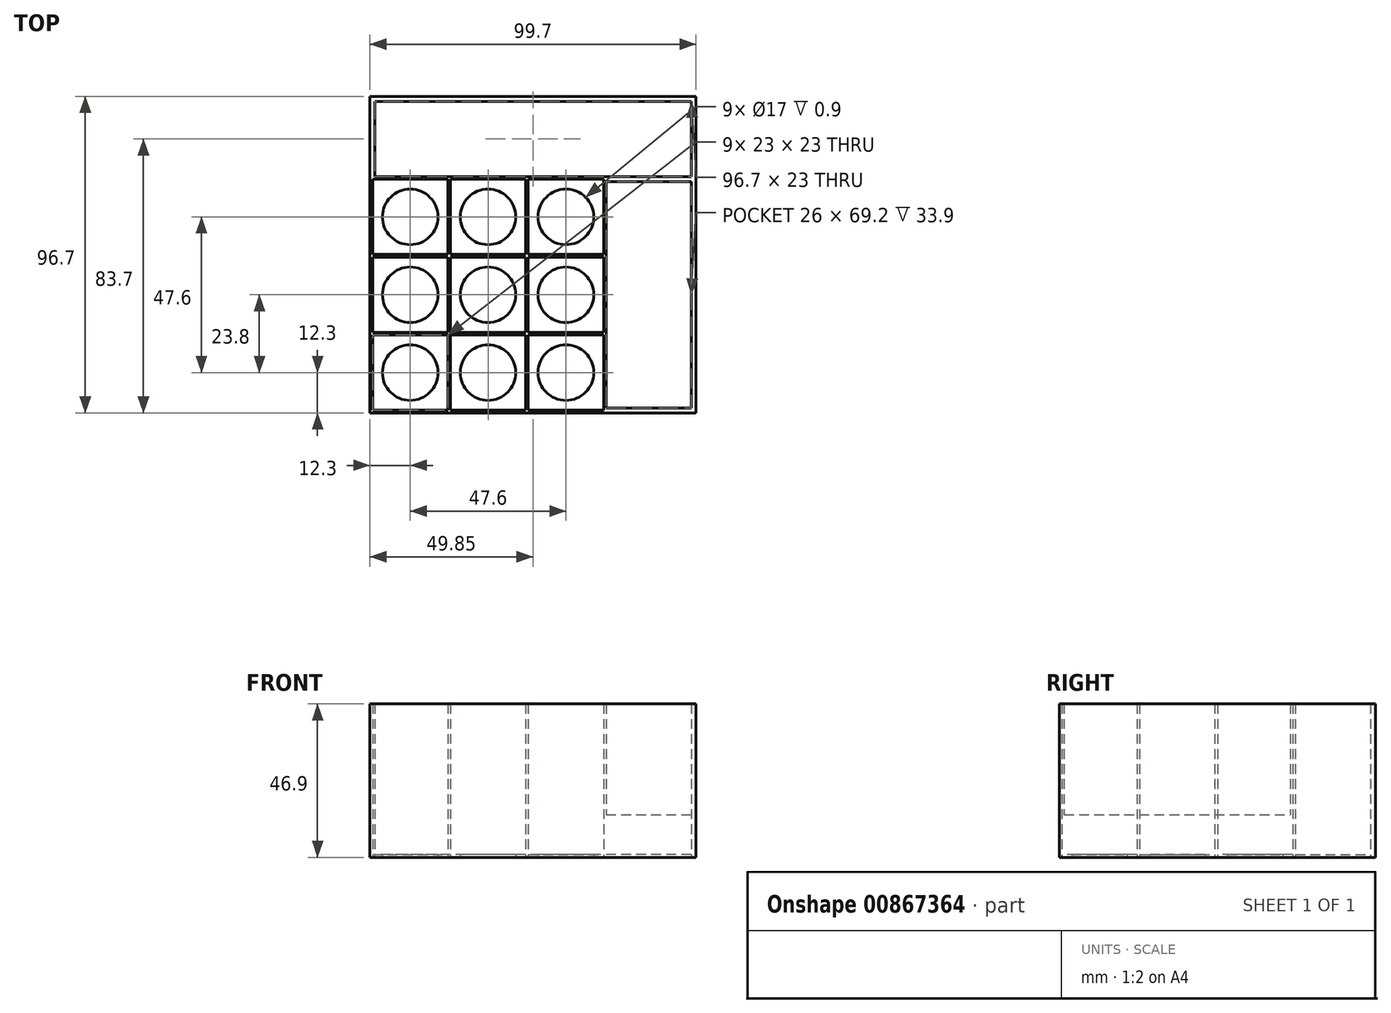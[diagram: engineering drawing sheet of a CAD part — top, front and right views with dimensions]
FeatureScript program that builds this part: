
annotation { "Feature Type Name" : "Feature", "Feature Type Description" : "" }
export const myFeature = defineFeature(function(context is Context, id is Id, definition is map)
    precondition{}
    {
        {
            var Q0;
            Q0=qCreatedBy(makeId("Top.planeOp"),FACE);
            var sketch = newSketch(context, id + "F0", { "sketchPlane" : qUnion([Q0])});
            skLineSegment(sketch, "E0", {"start": v(-36.1, 36.1) * mm, "end": v(-36.1, -36.1) * mm});
            skLineSegment(sketch, "E1", {"start": v(-36.1, -36.1) * mm, "end": v(36.1, -36.1) * mm});
            skLineSegment(sketch, "E2", {"start": v(36.1, -36.1) * mm, "end": v(36.1, 36.1) * mm});
            skLineSegment(sketch, "E3", {"start": v(36.1, 36.1) * mm, "end": v(-36.1, 36.1) * mm});
            skLineSegment(sketch, "E4.bottom", {"start": v(-35.3, 35.3) * mm, "end": v(-12.3, 35.3) * mm});
            skLineSegment(sketch, "E4.top", {"start": v(-35.3, 12.3) * mm, "end": v(-12.3, 12.3) * mm});
            skLineSegment(sketch, "E4.left", {"start": v(-35.3, 35.3) * mm, "end": v(-35.3, 12.3) * mm});
            skLineSegment(sketch, "E4.right", {"start": v(-12.3, 35.3) * mm, "end": v(-12.3, 12.3) * mm});
            skLineSegment(sketch, "E5", {"start": v(0, 86.02) * mm, "end": v(0, -32.75) * mm, "construction": true});
            skPoint(sketch, "E5.startSnap0", {"position": v(0, 36.1) * mm});
            skLineSegment(sketch, "E6", {"start": v(50.67, 0) * mm, "end": v(-45.02, 0) * mm, "construction": true});
            skPoint(sketch, "E6.startSnap0", {"position": v(36.1, 0) * mm});
            skPoint(sketch, "E7", {"position": v(0, 0) * mm});
            skLineSegment(sketch, "E8", {"start": v(-11.9, 47.3) * mm, "end": v(-11.9, -75.9) * mm, "construction": true});
            skLineSegment(sketch, "E9", {"start": v(-48.72, 11.9) * mm, "end": v(36.2, 11.9) * mm, "construction": true});
            skLineSegment(sketch, "E10.MirrorCS", {"start": v(-11.5, 35.3) * mm, "end": v(-11.5, 12.3) * mm});
            skLineSegment(sketch, "E11.MirrorCS", {"start": v(11.5, 35.3) * mm, "end": v(-11.5, 35.3) * mm});
            skLineSegment(sketch, "E12.MirrorCS", {"start": v(11.5, 35.3) * mm, "end": v(11.5, 12.3) * mm});
            skLineSegment(sketch, "E13.MirrorCS", {"start": v(11.5, 12.3) * mm, "end": v(-11.5, 12.3) * mm});
            skLineSegment(sketch, "E14", {"start": v(11.9, 49.65) * mm, "end": v(11.9, -75.25) * mm, "construction": true});
            skLineSegment(sketch, "E15.MirrorCS", {"start": v(12.3, 35.3) * mm, "end": v(12.3, 12.3) * mm});
            skLineSegment(sketch, "E16.MirrorCS", {"start": v(12.3, 35.3) * mm, "end": v(35.3, 35.3) * mm});
            skLineSegment(sketch, "E17.MirrorCS", {"start": v(35.3, 35.3) * mm, "end": v(35.3, 12.3) * mm});
            skLineSegment(sketch, "E18.MirrorCS", {"start": v(12.3, 12.3) * mm, "end": v(35.3, 12.3) * mm});
            skLineSegment(sketch, "E19.MirrorCS", {"start": v(-35.3, 11.5) * mm, "end": v(-12.3, 11.5) * mm});
            skLineSegment(sketch, "E20.MirrorCS", {"start": v(-12.3, -11.5) * mm, "end": v(-12.3, 11.5) * mm});
            skLineSegment(sketch, "E21.MirrorCS", {"start": v(-35.3, -11.5) * mm, "end": v(-12.3, -11.5) * mm});
            skLineSegment(sketch, "E22.MirrorCS", {"start": v(-35.3, -11.5) * mm, "end": v(-35.3, 11.5) * mm});
            skLineSegment(sketch, "E23.MirrorCS", {"start": v(-11.5, -11.5) * mm, "end": v(-11.5, 11.5) * mm});
            skLineSegment(sketch, "E24.MirrorCS", {"start": v(11.5, 11.5) * mm, "end": v(-11.5, 11.5) * mm});
            skLineSegment(sketch, "E25.MirrorCS", {"start": v(11.5, -11.5) * mm, "end": v(11.5, 11.5) * mm});
            skLineSegment(sketch, "E26.MirrorCS", {"start": v(11.5, -11.5) * mm, "end": v(-11.5, -11.5) * mm});
            skLineSegment(sketch, "E27.MirrorCS", {"start": v(12.3, -11.5) * mm, "end": v(35.3, -11.5) * mm});
            skLineSegment(sketch, "E28.MirrorCS", {"start": v(12.3, -11.5) * mm, "end": v(12.3, 11.5) * mm});
            skLineSegment(sketch, "E29.MirrorCS", {"start": v(12.3, 11.5) * mm, "end": v(35.3, 11.5) * mm});
            skLineSegment(sketch, "E30.MirrorCS", {"start": v(35.3, -11.5) * mm, "end": v(35.3, 11.5) * mm});
            skLineSegment(sketch, "E31", {"start": v(-45.02, -11.9) * mm, "end": v(46.48, -11.9) * mm, "construction": true});
            skLineSegment(sketch, "E32.MirrorCS", {"start": v(-35.3, -12.3) * mm, "end": v(-12.3, -12.3) * mm});
            skLineSegment(sketch, "E33.MirrorCS", {"start": v(-35.3, -12.3) * mm, "end": v(-35.3, -35.3) * mm});
            skLineSegment(sketch, "E34.MirrorCS", {"start": v(-35.3, -35.3) * mm, "end": v(-12.3, -35.3) * mm});
            skLineSegment(sketch, "E35.MirrorCS", {"start": v(-12.3, -12.3) * mm, "end": v(-12.3, -35.3) * mm});
            skLineSegment(sketch, "E36.MirrorCS", {"start": v(11.5, -12.3) * mm, "end": v(-11.5, -12.3) * mm});
            skLineSegment(sketch, "E37.MirrorCS", {"start": v(-11.5, -12.3) * mm, "end": v(-11.5, -35.3) * mm});
            skLineSegment(sketch, "E38.MirrorCS", {"start": v(11.5, -35.3) * mm, "end": v(-11.5, -35.3) * mm});
            skLineSegment(sketch, "E39.MirrorCS", {"start": v(11.5, -12.3) * mm, "end": v(11.5, -35.3) * mm});
            skLineSegment(sketch, "E40.MirrorCS", {"start": v(12.3, -12.3) * mm, "end": v(12.3, -35.3) * mm});
            skLineSegment(sketch, "E41.MirrorCS", {"start": v(12.3, -12.3) * mm, "end": v(35.3, -12.3) * mm});
            skLineSegment(sketch, "E42.MirrorCS", {"start": v(35.3, -12.3) * mm, "end": v(35.3, -35.3) * mm});
            skLineSegment(sketch, "E43.MirrorCS", {"start": v(12.3, -35.3) * mm, "end": v(35.3, -35.3) * mm});
            skLineSegment(sketch, "E44", {"start": v(36.1, 36.1) * mm, "end": v(63.6, 36.1) * mm});
            skLineSegment(sketch, "E45", {"start": v(63.6, 36.1) * mm, "end": v(63.6, -36.1) * mm});
            skLineSegment(sketch, "E46", {"start": v(63.6, -36.1) * mm, "end": v(36.1, -36.1) * mm});
            skLineSegment(sketch, "E47", {"start": v(-36.1, 36.1) * mm, "end": v(-36.1, 60.6) * mm});
            skLineSegment(sketch, "E48", {"start": v(-36.1, 60.6) * mm, "end": v(63.6, 60.6) * mm});
            skLineSegment(sketch, "E49", {"start": v(63.6, 60.6) * mm, "end": v(63.6, 36.1) * mm});
            skLineSegment(sketch, "E50", {"start": v(-38.02, 23.8) * mm, "end": v(-9.58, 23.8) * mm, "construction": true});
            skPoint(sketch, "E50.startSnap0", {"position": v(-35.3, 23.8) * mm});
            skPoint(sketch, "E50.endSnap0", {"position": v(-11.5, 23.8) * mm});
            skCircle(sketch, "E51", {"center": v(-23.8, 23.8) * mm, "radius": 8.5 * mm});
            skCircle(sketch, "E52.MirrorC", {"center": v(0, 23.8) * mm, "radius": 8.5 * mm});
            skCircle(sketch, "E53.MirrorC", {"center": v(23.8, 23.8) * mm, "radius": 8.5 * mm});
            skCircle(sketch, "E54.MirrorC", {"center": v(-23.8, 0) * mm, "radius": 8.5 * mm});
            skCircle(sketch, "E55.MirrorC", {"center": v(0, 0) * mm, "radius": 8.5 * mm});
            skCircle(sketch, "E56.MirrorC", {"center": v(23.8, 0) * mm, "radius": 8.5 * mm});
            skCircle(sketch, "E57.MirrorC", {"center": v(-23.8, -23.8) * mm, "radius": 8.5 * mm});
            skCircle(sketch, "E58.MirrorC", {"center": v(0, -23.8) * mm, "radius": 8.5 * mm});
            skCircle(sketch, "E59.MirrorC", {"center": v(23.8, -23.8) * mm, "radius": 8.5 * mm});
            skLineSegment(sketch, "E60.0", {"start": v(62.1, -34.6) * mm, "end": v(35.8, -34.6) * mm});
            skLineSegment(sketch, "E60.1", {"start": v(62.1, 34.6) * mm, "end": v(62.1, -34.6) * mm});
            skLineSegment(sketch, "E60.2", {"start": v(35.7, 34.6) * mm, "end": v(62.1, 34.6) * mm});
            skLineSegment(sketch, "E61.0", {"start": v(62.1, 59.1) * mm, "end": v(62.1, 36.9) * mm});
            skLineSegment(sketch, "E61.1", {"start": v(-34.6, 59.1) * mm, "end": v(62.1, 59.1) * mm});
            skLineSegment(sketch, "E61.2", {"start": v(-34.6, 36.9) * mm, "end": v(-34.6, 59.1) * mm});
            skLineSegment(sketch, "E62", {"start": v(-34.6, 36.9) * mm, "end": v(-34.6, 36.1) * mm});
            skLineSegment(sketch, "E63", {"start": v(62.1, 36.9) * mm, "end": v(62.1, 36.1) * mm});
            skLineSegment(sketch, "E64", {"start": v(36.1, 34.6) * mm, "end": v(35.7, 34.6) * mm});
            skLineSegment(sketch, "E65", {"start": v(36.1, -34.6) * mm, "end": v(35.8, -34.6) * mm});
            skLineSegment(sketch, "E66", {"start": v(-23.8, 38.74) * mm, "end": v(-23.8, 9.64) * mm, "construction": true});
            skPoint(sketch, "E66.startSnap0", {"position": v(-23.8, 35.3) * mm});
            skPoint(sketch, "E66.endSnap0", {"position": v(-23.8, 11.5) * mm});
            skSolve(sketch);
        }
        {
            var Q0;
            Q0=makeQuery(id+"F0.imprint","IMPRINT",FACE,{"disambiguationData":[TD([[makeQuery(id+"F0.imprint","IMPRINT",EDGE,{"derivedFrom":sQuery(id+"F0.wireOp",EDGE,"E4.bottom")}),-1.0]])]});
            var Q1;
            Q1=makeQuery(id+"F0.imprint","IMPRINT",FACE,{"disambiguationData":[TD([[makeQuery(id+"F0.imprint","IMPRINT",EDGE,{"derivedFrom":sQuery(id+"F0.wireOp",EDGE,"E10.MirrorCS")}),1.0]])]});
            var Q2;
            Q2=makeQuery(id+"F0.imprint","IMPRINT",FACE,{"disambiguationData":[TD([[makeQuery(id+"F0.imprint","IMPRINT",EDGE,{"derivedFrom":sQuery(id+"F0.wireOp",EDGE,"E15.MirrorCS")}),1.0]])]});
            var Q3;
            Q3=makeQuery(id+"F0.imprint","IMPRINT",FACE,{"disambiguationData":[TD([[makeQuery(id+"F0.imprint","IMPRINT",EDGE,{"derivedFrom":sQuery(id+"F0.wireOp",EDGE,"E27.MirrorCS")}),1.0]])]});
            var Q4;
            Q4=makeQuery(id+"F0.imprint","IMPRINT",FACE,{"disambiguationData":[TD([[makeQuery(id+"F0.imprint","IMPRINT",EDGE,{"derivedFrom":sQuery(id+"F0.wireOp",EDGE,"E23.MirrorCS")}),-1.0]])]});
            var Q5;
            Q5=makeQuery(id+"F0.imprint","IMPRINT",FACE,{"disambiguationData":[TD([[makeQuery(id+"F0.imprint","IMPRINT",EDGE,{"derivedFrom":sQuery(id+"F0.wireOp",EDGE,"E19.MirrorCS")}),-1.0]])]});
            var Q6;
            Q6=makeQuery(id+"F0.imprint","IMPRINT",FACE,{"disambiguationData":[TD([[makeQuery(id+"F0.imprint","IMPRINT",EDGE,{"derivedFrom":sQuery(id+"F0.wireOp",EDGE,"E32.MirrorCS")}),-1.0]])]});
            var Q7;
            Q7=makeQuery(id+"F0.imprint","IMPRINT",FACE,{"disambiguationData":[TD([[makeQuery(id+"F0.imprint","IMPRINT",EDGE,{"derivedFrom":sQuery(id+"F0.wireOp",EDGE,"E36.MirrorCS")}),1.0]])]});
            var Q8;
            Q8=makeQuery(id+"F0.imprint","IMPRINT",FACE,{"disambiguationData":[TD([[makeQuery(id+"F0.imprint","IMPRINT",EDGE,{"derivedFrom":sQuery(id+"F0.wireOp",EDGE,"E40.MirrorCS")}),1.0]])]});
            var Q9;
            Q9=makeQuery(id+"F0.imprint","IMPRINT",FACE,{"disambiguationData":[TD([[makeQuery(id+"F0.imprint","IMPRINT",EDGE,{"derivedFrom":sQuery(id+"F0.wireOp",EDGE,"E61.0")}),-1.0]])]});
            extrude(context, id + "F1", {"entities" : qUnion([Q0, Q1, Q2, Q3, Q4, Q5, Q6, Q7, Q8, Q9]), "depth" : .9 * mm, "offsetDistance" : 25 * mm});
        }
        {
            var Q0;
            {var subQ0=sQuery(id+"F0.wireOp",EDGE,"E47");Q0=makeQuery(id+"F0.imprint","IMPRINT",FACE,{"disambiguationData":[TD([[makeQuery(id+"F0.imprint","IMPRINT",EDGE,{"derivedFrom":subQ0}),-1.0]])]});}
            var Q1;
            {var subQ4=sQuery(id+"F0.wireOp",EDGE,"E45");Q1=makeQuery(id+"F0.imprint","IMPRINT",FACE,{"disambiguationData":[TD([[makeQuery(id+"F0.imprint","IMPRINT",EDGE,{"derivedFrom":subQ4}),-1.0]])]});}
            var Q2;
            {var subQ4=sQuery(id+"F0.wireOp",EDGE,"E0");Q2=makeQuery(id+"F0.imprint","IMPRINT",FACE,{"disambiguationData":[TD([[makeQuery(id+"F0.imprint","IMPRINT",EDGE,{"derivedFrom":subQ4}),1.0]])]});}
            extrude(context, id + "F2", {"entities" : qUnion([Q0, Q1, Q2]), "depth" : 46.9 * mm, "offsetDistance" : 25 * mm});
        }
        {
            var Q0;
            Q0=makeQuery(id+"F0.imprint","IMPRINT",FACE,{"disambiguationData":[TD([[makeQuery(id+"F0.imprint","IMPRINT",EDGE,{"derivedFrom":sQuery(id+"F0.wireOp",EDGE,"E60.0")}),-1.0]])]});
            extrude(context, id + "F3", {"entities" : qUnion([Q0]), "operationType" : NewBodyOperationType.ADD, "depth" : 13 * mm, "offsetDistance" : 25 * mm});
        }
    });
